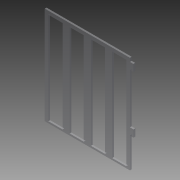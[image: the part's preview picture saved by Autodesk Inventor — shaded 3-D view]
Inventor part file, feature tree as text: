
AUTODESK INVENTOR PART (.ipt)
format: ipt  version: 2013 (Build 170138000, 138)  size: 134,656 bytes
history: native  units: in
note: dims shown in document units (in); Inventor stores cm internally (conversion verified against a paired STEP export)
features: extrude x4, sketch x4
ambient origin geometry x8: Origin, YZ Plane, XZ Plane, XY Plane, X Axis, Y Axis, Z Axis, Center Point
bodies: Solid1 (feature_tree)
feature tree (8):
  extrude  "Extrusion1"  Depth=6.0in
  extrude  "Extrusion2"  Depth=0.25in
  extrude  "Extrusion3"  Depth=0.25in
  extrude  "Extrusion4"  Depth=3.5in
  sketch  "Sketch1"  dims[d0=7.0in d1=6.0in]
  sketch  "Sketch2"  dims[d7=0.125in d8=0.0in d9=0.25in]
  sketch  "Sketch3"  dims[d10=0.5in d11=0.25in]
  sketch  "Sketch4"  dims[d12=0.5in d13=3.5in d14=0.25in d15=0.125in d16=0.0in d17=1.0in d18=1.0in d20=0.25in d21=0.25in d22=0.25in d23=1.5748in d25=1.5in d26=0.3937in d28=1.0in d30=0.125in d31=0.0in d32=0.15in d33=1.0in d34=0.0in]
